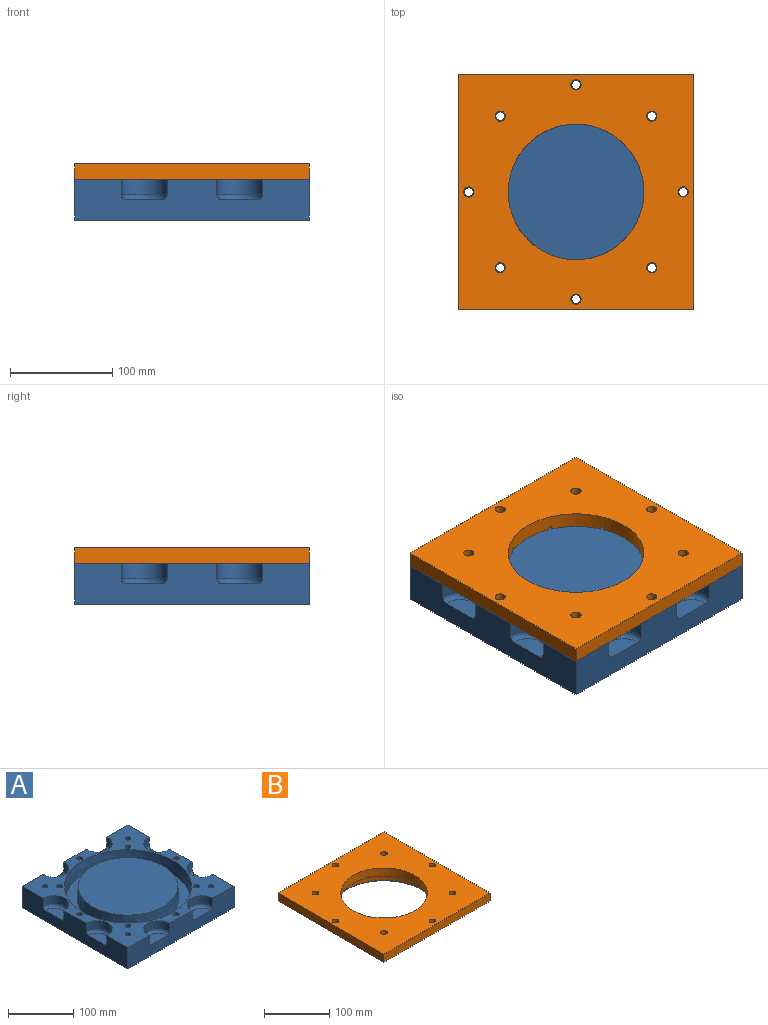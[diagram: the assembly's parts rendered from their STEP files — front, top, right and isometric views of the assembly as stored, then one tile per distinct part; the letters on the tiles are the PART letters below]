
ASSEMBLY  parts=2 mates=1
PART A: 46 faces, bbox 231.4x231.4x40 mm
  f0: plane 230x40mm, normal (0,1,0), area 7427.5mm2, adj f1,f15,f16,f17,f34,f35,f36,f37
  f1: plane 230x40mm, normal (-1,0,0), area 7427.5mm2, adj f0,f2,f16,f17,f30,f31,f32,f33
  f2: plane 230x40mm, normal (0,-1,0), area 7427.5mm2, adj f1,f15,f16,f17,f26,f27,f28,f29
  f3: cylinder r=4.3mm len=40mm, axis (0,0,1), area 1080.7mm2, adj f16,f17
  f4: cylinder r=4.3mm len=40mm, axis (0,0,1), area 1080.7mm2, adj f16,f17
  f5: cylinder r=4.3mm len=40mm, axis (0,0,1), area 1080.7mm2, adj f16,f17
  f6: cylinder r=4.3mm len=40mm, axis (0,0,1), area 1080.7mm2, adj f16,f17
  f7: cylinder r=4.3mm len=40mm, axis (0,0,1), area 1080.7mm2, adj f16,f17
  f8: cylinder r=4.3mm len=40mm, axis (0,0,1), area 1080.7mm2, adj f16,f17
  f9: cylinder r=4.3mm len=40mm, axis (0,0,1), area 1080.7mm2, adj f16,f17
  f10: cylinder r=4.3mm len=40mm, axis (0,0,1), area 1080.7mm2, adj f16,f17
  f11: cylinder r=4.3mm len=40mm, axis (0,0,1), area 1080.7mm2, adj f16,f17
  f12: cylinder r=4.3mm len=40mm, axis (0,0,1), area 1080.7mm2, adj f16,f17
  f13: cylinder r=4.3mm len=40mm, axis (0,0,1), area 1080.7mm2, adj f16,f17
  f14: cylinder r=4.3mm len=40mm, axis (0,0,1), area 1080.7mm2, adj f16,f17
  f15: plane 230x40mm, normal (1,0,0), area 7427.5mm2, adj f0,f2,f16,f17,f22,f23,f24,f25
  f16: plane 230x230mm, normal (0,0,-1), area 52202.9mm2, adj f0,f1,f2,f3,f4,f5,f6,f7
  f17: plane 230x230mm, normal (0,0,1), area 15320.3mm2, adj f0,f1,f2,f3,f4,f5,f6,f7
  f18: cone r=76.5mm half-angle=3deg, axis (0,0,-1), area 12136.1mm2, adj f20,f21
  f19: cone r=97.5mm half-angle=3deg, axis (0,0,1), area 15233.2mm2, adj f17,f20
  f20: plane 192.38x192.38mm, normal (0,0,1), area 10047mm2, adj f18,f19
  f21: plane 153x153mm, normal (0,0,1), area 18385.4mm2, adj f18
  f22: plane 35x19.32mm, normal (0,0,1), area 544.8mm2, adj f15,f43
  f23: cylinder r=22.5mm len=45mm, axis (0,0,1), area 1115.1mm2, adj f15,f17,f43
  f24: plane 35x19.32mm, normal (0,0,1), area 544.8mm2, adj f15,f42
  f25: cylinder r=22.5mm len=45mm, axis (0,0,1), area 1115.1mm2, adj f15,f17,f42
  f26: cylinder r=22.5mm len=45mm, axis (0,0,1), area 1115.1mm2, adj f2,f17,f45
  f27: plane 35x19.32mm, normal (0,0,1), area 544.8mm2, adj f2,f45
  f28: cylinder r=22.5mm len=45mm, axis (0,0,1), area 1115.1mm2, adj f2,f17,f44
  f29: plane 35x19.32mm, normal (0,0,1), area 544.8mm2, adj f2,f44
  f30: cylinder r=22.5mm len=45mm, axis (0,0,1), area 1115.1mm2, adj f1,f17,f39
  f31: plane 35x19.32mm, normal (0,0,1), area 544.8mm2, adj f1,f39
  f32: cylinder r=22.5mm len=45mm, axis (0,0,1), area 1115.1mm2, adj f1,f17,f38
  f33: plane 35x19.32mm, normal (0,0,1), area 544.8mm2, adj f1,f38
  f34: plane 35x19.32mm, normal (0,0,1), area 544.8mm2, adj f0,f41
  f35: cylinder r=22.5mm len=45mm, axis (0,0,1), area 1115.1mm2, adj f0,f17,f41
  f36: plane 35x19.32mm, normal (0,0,1), area 544.8mm2, adj f0,f40
  f37: cylinder r=22.5mm len=45mm, axis (0,0,1), area 1115.1mm2, adj f0,f17,f40
  f38: torus R=17.5mm, axis (0,0,1), area 539mm2, adj f1,f32,f33
  f39: torus R=17.5mm, axis (0,0,1), area 539mm2, adj f1,f30,f31
  f40: torus R=17.5mm, axis (0,0,1), area 539mm2, adj f0,f36,f37
  f41: torus R=17.5mm, axis (0,0,1), area 539mm2, adj f0,f34,f35
  f42: torus R=17.5mm, axis (0,0,1), area 539mm2, adj f15,f24,f25
  f43: torus R=17.5mm, axis (0,0,1), area 539mm2, adj f15,f22,f23
  f44: torus R=17.5mm, axis (0,0,1), area 539mm2, adj f2,f28,f29
  f45: torus R=17.5mm, axis (0,0,1), area 539mm2, adj f2,f26,f27
PART B: 152 faces, bbox 230x230x35 mm
  f0: plane 161x161mm, normal (0,0,-1), area 1814.9mm2, adj f24,f25,f26,f27,f28,f29,f30,f31
  f1: plane 230x230mm, normal (0,0,-1), area 22138.5mm2, adj f11,f12,f13,f14,f15,f16,f17,f18
  f2: plane 43.26x43.26mm, normal (0,0,-1), area 531.6mm2, adj f9,f36,f57,f61,f100,f101
  f3: plane 55.77x14.5mm, normal (0,0,-1), area 531.6mm2, adj f9,f38,f94,f95,f102,f103
  f4: plane 43.26x43.26mm, normal (0,0,-1), area 531.6mm2, adj f9,f24,f89,f90,f96,f97
  f5: plane 55.77x14.5mm, normal (0,0,-1), area 531.6mm2, adj f9,f26,f83,f84,f87,f91
  f6: plane 43.26x43.26mm, normal (0,0,-1), area 531.6mm2, adj f9,f28,f77,f78,f81,f85
  f7: plane 55.77x14.5mm, normal (0,0,-1), area 531.6mm2, adj f9,f30,f71,f72,f75,f79
  f8: plane 43.26x43.26mm, normal (0,0,-1), area 531.6mm2, adj f9,f32,f65,f66,f69,f73
  f9: cylinder r=66.5mm len=133mm, axis (0,0,-1), area 6195.5mm2, adj f2,f3,f4,f5,f6,f7,f8,f10
  f10: plane 55.77x14.5mm, normal (0,0,-1), area 531.6mm2, adj f9,f34,f59,f60,f63,f67
  f11: plane 230x15mm, normal (0,1,0), area 3450mm2, adj f1,f12,f14,f23
  f12: plane 230x15mm, normal (-1,0,0), area 3450mm2, adj f1,f11,f13,f23
  f13: plane 230x15mm, normal (0,-1,0), area 3450mm2, adj f1,f12,f14,f23
  f14: plane 230x15mm, normal (1,0,0), area 3450mm2, adj f1,f11,f13,f23
  f15: cylinder r=5mm len=15mm, axis (0,0,-1), area 471.2mm2, adj f1,f23
  f16: cylinder r=5mm len=15mm, axis (0,0,-1), area 471.2mm2, adj f1,f23
  f17: cylinder r=5mm len=15mm, axis (0,0,-1), area 471.2mm2, adj f1,f23
  f18: cylinder r=5mm len=15mm, axis (0,0,-1), area 471.2mm2, adj f1,f23
  f19: cylinder r=5mm len=15mm, axis (0,0,-1), area 471.2mm2, adj f1,f23
  f20: cylinder r=5mm len=15mm, axis (0,0,-1), area 471.2mm2, adj f1,f23
  f21: cylinder r=5mm len=15mm, axis (0,0,-1), area 471.2mm2, adj f1,f23
  f22: cylinder r=5mm len=15mm, axis (0,0,-1), area 471.2mm2, adj f1,f23
  f23: plane 230x230mm, normal (0,0,1), area 38378.8mm2, adj f9,f11,f12,f13,f14,f15,f16,f17
  f24: cone r=76.5mm half-angle=3deg, axis (0,0,-1), area 285.1mm2, adj f0,f4,f25,f55
  f25: cone r=1.5mm half-angle=3deg, axis (0,0,-1), area 24.6mm2, adj f0,f24,f26,f88
  f26: cone r=76.5mm half-angle=3deg, axis (0,0,-1), area 285.1mm2, adj f0,f5,f25,f27
  f27: cone r=1.5mm half-angle=3deg, axis (0,0,-1), area 24.6mm2, adj f0,f26,f28,f82
  f28: cone r=76.5mm half-angle=3deg, axis (0,0,-1), area 285.1mm2, adj f0,f6,f27,f29
  f29: cone r=1.5mm half-angle=3deg, axis (0,0,-1), area 24.6mm2, adj f0,f28,f30,f76
  f30: cone r=76.5mm half-angle=3deg, axis (0,0,-1), area 285.1mm2, adj f0,f7,f29,f31
  f31: cone r=1.5mm half-angle=3deg, axis (0,0,-1), area 24.6mm2, adj f0,f30,f32,f70
  f32: cone r=76.5mm half-angle=3deg, axis (0,0,-1), area 285.1mm2, adj f0,f8,f31,f33
  f33: cone r=1.5mm half-angle=3deg, axis (0,0,-1), area 24.6mm2, adj f0,f32,f34,f64
  f34: cone r=76.5mm half-angle=3deg, axis (0,0,-1), area 285.1mm2, adj f0,f10,f33,f35
  f35: cone r=1.5mm half-angle=3deg, axis (0,0,-1), area 24.6mm2, adj f0,f34,f36,f58
  f36: cone r=76.5mm half-angle=3deg, axis (0,0,-1), area 285.1mm2, adj f0,f2,f35,f37
  f37: cone r=1.5mm half-angle=3deg, axis (0,0,-1), area 24.6mm2, adj f0,f36,f38,f99
  f38: cone r=76.5mm half-angle=3deg, axis (0,0,-1), area 285.1mm2, adj f0,f3,f37,f55
  f39: cone r=1.5mm half-angle=3deg, axis (0,0,-1), area 24.3mm2, adj f40,f54,f56,f111
  f40: cone r=97.5mm half-angle=3deg, axis (0,0,1), area 366.7mm2, adj f1,f39,f41,f56
  f41: cone r=1.5mm half-angle=3deg, axis (0,0,-1), area 24.3mm2, adj f40,f42,f56,f106
  f42: cone r=97.5mm half-angle=3deg, axis (0,0,1), area 366.7mm2, adj f1,f41,f43,f56
  f43: cone r=1.5mm half-angle=3deg, axis (0,0,-1), area 24.3mm2, adj f42,f44,f56,f141
  f44: cone r=97.5mm half-angle=3deg, axis (0,0,1), area 366.7mm2, adj f1,f43,f45,f56
  f45: cone r=1.5mm half-angle=3deg, axis (0,0,-1), area 24.3mm2, adj f44,f46,f56,f136
  f46: cone r=97.5mm half-angle=3deg, axis (0,0,1), area 366.7mm2, adj f1,f45,f47,f56
  f47: cone r=1.5mm half-angle=3deg, axis (0,0,-1), area 24.3mm2, adj f46,f48,f56,f131
  f48: cone r=97.5mm half-angle=3deg, axis (0,0,1), area 366.7mm2, adj f1,f47,f49,f56
  f49: cone r=1.5mm half-angle=3deg, axis (0,0,-1), area 24.3mm2, adj f48,f50,f56,f126
  f50: cone r=97.5mm half-angle=3deg, axis (0,0,1), area 366.7mm2, adj f1,f49,f51,f56
  f51: cone r=1.5mm half-angle=3deg, axis (0,0,-1), area 24.3mm2, adj f50,f52,f56,f121
  f52: cone r=97.5mm half-angle=3deg, axis (0,0,1), area 366.7mm2, adj f1,f51,f53,f56
  f53: cone r=1.5mm half-angle=3deg, axis (0,0,-1), area 24.3mm2, adj f52,f54,f56,f116
  f54: cone r=97.5mm half-angle=3deg, axis (0,0,1), area 366.7mm2, adj f1,f39,f53,f56
  f55: cone r=1.5mm half-angle=3deg, axis (0,0,-1), area 24.6mm2, adj f0,f24,f38,f93
  f56: plane 194.48x194.48mm, normal (0,0,-1), area 2208.4mm2, adj f39,f40,f41,f42,f43,f44,f45,f46
  f57: plane 9.23x3.82mm, normal (0.38,0.92,0), area 30mm2, adj f2,f58,f61,f62
  f58: cylinder r=1.5mm len=3mm, axis (0,0,-1), area 14.2mm2, adj f35,f57,f59,f62
  f59: plane 9.23x3.82mm, normal (-0.38,-0.92,0), area 30mm2, adj f10,f58,f60,f62
  f60: cylinder r=1.5mm len=3mm, axis (0,0,-1), area 0.1mm2, adj f9,f10,f59,f62
  f61: cylinder r=1.5mm len=3mm, axis (0,0,-1), area 0.1mm2, adj f2,f9,f57,f62
  f62: plane 11.33x6.72mm, normal (0,0,-1), area 33.6mm2, adj f9,f57,f58,f59,f60,f61
  f63: plane 9.23x3.82mm, normal (-0.38,0.92,0), area 30mm2, adj f10,f64,f67,f68
  f64: cylinder r=1.5mm len=3mm, axis (0,0,-1), area 14.2mm2, adj f33,f63,f65,f68
  f65: plane 9.23x3.82mm, normal (0.38,-0.92,0), area 30mm2, adj f8,f64,f66,f68
  f66: cylinder r=1.5mm len=3mm, axis (0,0,-1), area 0.1mm2, adj f8,f9,f65,f68
  f67: cylinder r=1.5mm len=3mm, axis (0,0,-1), area 0.1mm2, adj f9,f10,f63,f68
  f68: plane 11.33x6.72mm, normal (0,0,-1), area 33.6mm2, adj f9,f63,f64,f65,f66,f67
  f69: plane 9.23x3.82mm, normal (-0.92,0.38,0), area 30mm2, adj f8,f70,f73,f74
  f70: cylinder r=1.5mm len=3mm, axis (0,0,-1), area 14.2mm2, adj f31,f69,f71,f74
  f71: plane 9.23x3.82mm, normal (0.92,-0.38,0), area 30mm2, adj f7,f70,f72,f74
  f72: cylinder r=1.5mm len=3mm, axis (0,0,-1), area 0.1mm2, adj f7,f9,f71,f74
  f73: cylinder r=1.5mm len=3mm, axis (0,0,-1), area 0.1mm2, adj f8,f9,f69,f74
  f74: plane 11.33x6.72mm, normal (0,0,-1), area 33.6mm2, adj f9,f69,f70,f71,f72,f73
  f75: plane 9.23x3.82mm, normal (-0.92,-0.38,0), area 30mm2, adj f7,f76,f79,f80
  f76: cylinder r=1.5mm len=3mm, axis (0,0,-1), area 14.2mm2, adj f29,f75,f77,f80
  f77: plane 9.23x3.82mm, normal (0.92,0.38,0), area 30mm2, adj f6,f76,f78,f80
  f78: cylinder r=1.5mm len=3mm, axis (0,0,-1), area 0.1mm2, adj f6,f9,f77,f80
  f79: cylinder r=1.5mm len=3mm, axis (0,0,-1), area 0.1mm2, adj f7,f9,f75,f80
  f80: plane 11.33x6.72mm, normal (0,0,-1), area 33.6mm2, adj f9,f75,f76,f77,f78,f79
  f81: plane 9.23x3.82mm, normal (-0.38,-0.92,0), area 30mm2, adj f6,f82,f85,f86
  f82: cylinder r=1.5mm len=3mm, axis (0,0,-1), area 14.2mm2, adj f27,f81,f83,f86
  f83: plane 9.23x3.82mm, normal (0.38,0.92,0), area 30mm2, adj f5,f82,f84,f86
  f84: cylinder r=1.5mm len=3mm, axis (0,0,-1), area 0.1mm2, adj f5,f9,f83,f86
  f85: cylinder r=1.5mm len=3mm, axis (0,0,-1), area 0.1mm2, adj f6,f9,f81,f86
  f86: plane 11.33x6.72mm, normal (0,0,-1), area 33.6mm2, adj f9,f81,f82,f83,f84,f85
  f87: plane 9.23x3.82mm, normal (0.38,-0.92,0), area 30mm2, adj f5,f88,f91,f92
  f88: cylinder r=1.5mm len=3mm, axis (0,0,-1), area 14.2mm2, adj f25,f87,f89,f92
  f89: plane 9.23x3.82mm, normal (-0.38,0.92,0), area 30mm2, adj f4,f88,f90,f92
  f90: cylinder r=1.5mm len=3mm, axis (0,0,-1), area 0.1mm2, adj f4,f9,f89,f92
  f91: cylinder r=1.5mm len=3mm, axis (0,0,-1), area 0.1mm2, adj f5,f9,f87,f92
  f92: plane 11.33x6.72mm, normal (0,0,-1), area 33.6mm2, adj f9,f87,f88,f89,f90,f91
  f93: cylinder r=1.5mm len=3mm, axis (0,0,-1), area 14.2mm2, adj f55,f94,f97,f98
  f94: plane 9.23x3.82mm, normal (-0.92,0.38,0), area 30mm2, adj f3,f93,f95,f98
  f95: cylinder r=1.5mm len=3mm, axis (0,0,-1), area 0.1mm2, adj f3,f9,f94,f98
  f96: cylinder r=1.5mm len=3mm, axis (0,0,-1), area 0.1mm2, adj f4,f9,f97,f98
  f97: plane 9.23x3.82mm, normal (0.92,-0.38,0), area 30mm2, adj f4,f93,f96,f98
  f98: plane 11.33x6.72mm, normal (0,0,-1), area 33.6mm2, adj f9,f93,f94,f95,f96,f97
  f99: cylinder r=1.5mm len=3mm, axis (0,0,-1), area 14.2mm2, adj f37,f100,f103,f104
  f100: plane 9.23x3.82mm, normal (-0.92,-0.38,0), area 30mm2, adj f2,f99,f101,f104
  f101: cylinder r=1.5mm len=3mm, axis (0,0,-1), area 0.1mm2, adj f2,f9,f100,f104
  f102: cylinder r=1.5mm len=3mm, axis (0,0,-1), area 0.1mm2, adj f3,f9,f103,f104
  f103: plane 9.23x3.82mm, normal (0.92,0.38,0), area 30mm2, adj f3,f99,f102,f104
  f104: plane 11.33x6.72mm, normal (0,0,-1), area 33.6mm2, adj f9,f99,f100,f101,f102,f103
  f105: plane 9.25x3.83mm, normal (-0.38,-0.92,0), area 30mm2, adj f1,f106,f108,f109
  f106: cylinder r=1.5mm len=3mm, axis (0,0,-1), area 14.1mm2, adj f1,f41,f105,f107,f109
  f107: plane 9.24x3.83mm, normal (0.38,0.92,0), area 30mm2, adj f1,f106,f108,f109
  f108: cylinder r=1.5mm len=3mm, axis (0,0,-1), area 14.1mm2, adj f1,f105,f107,f109
  f109: plane 12.24x6.83mm, normal (0,0,-1), area 37.1mm2, adj f105,f106,f107,f108
  f110: plane 9.25x3.83mm, normal (-0.92,-0.38,0), area 30mm2, adj f1,f111,f113,f114
  f111: cylinder r=1.5mm len=3mm, axis (0,0,-1), area 14.1mm2, adj f1,f39,f110,f112,f114
  f112: plane 9.24x3.83mm, normal (0.92,0.38,0), area 30mm2, adj f1,f111,f113,f114
  f113: cylinder r=1.5mm len=3mm, axis (0,0,-1), area 14.1mm2, adj f1,f110,f112,f114
  f114: plane 12.24x6.83mm, normal (0,0,-1), area 37.1mm2, adj f110,f111,f112,f113
  f115: plane 9.25x3.83mm, normal (-0.92,0.38,0), area 30mm2, adj f1,f116,f118,f119
  f116: cylinder r=1.5mm len=3mm, axis (0,0,-1), area 14.1mm2, adj f1,f53,f115,f117,f119
  f117: plane 9.24x3.83mm, normal (0.92,-0.38,0), area 30mm2, adj f1,f116,f118,f119
  f118: cylinder r=1.5mm len=3mm, axis (0,0,-1), area 14.1mm2, adj f1,f115,f117,f119
  f119: plane 12.24x6.83mm, normal (0,0,-1), area 37.1mm2, adj f115,f116,f117,f118
  f120: plane 9.25x3.83mm, normal (-0.38,0.92,0), area 30mm2, adj f1,f121,f123,f124
  f121: cylinder r=1.5mm len=3mm, axis (0,0,-1), area 14.1mm2, adj f1,f51,f120,f122,f124
  f122: plane 9.24x3.83mm, normal (0.38,-0.92,0), area 30mm2, adj f1,f121,f123,f124
  f123: cylinder r=1.5mm len=3mm, axis (0,0,-1), area 14.1mm2, adj f1,f120,f122,f124
  f124: plane 12.24x6.83mm, normal (0,0,-1), area 37.1mm2, adj f120,f121,f122,f123
  f125: plane 9.25x3.83mm, normal (0.38,0.92,0), area 30mm2, adj f1,f126,f128,f129
  f126: cylinder r=1.5mm len=3mm, axis (0,0,-1), area 14.1mm2, adj f1,f49,f125,f127,f129
  f127: plane 9.24x3.83mm, normal (-0.38,-0.92,0), area 30mm2, adj f1,f126,f128,f129
  f128: cylinder r=1.5mm len=3mm, axis (0,0,-1), area 14.1mm2, adj f1,f125,f127,f129
  f129: plane 12.24x6.83mm, normal (0,0,-1), area 37.1mm2, adj f125,f126,f127,f128
  f130: plane 9.25x3.83mm, normal (0.92,0.38,0), area 30mm2, adj f1,f131,f133,f134
  f131: cylinder r=1.5mm len=3mm, axis (0,0,-1), area 14.1mm2, adj f1,f47,f130,f132,f134
  f132: plane 9.24x3.83mm, normal (-0.92,-0.38,0), area 30mm2, adj f1,f131,f133,f134
  f133: cylinder r=1.5mm len=3mm, axis (0,0,-1), area 14.1mm2, adj f1,f130,f132,f134
  f134: plane 12.24x6.83mm, normal (0,0,-1), area 37.1mm2, adj f130,f131,f132,f133
  f135: plane 9.25x3.83mm, normal (0.92,-0.38,0), area 30mm2, adj f1,f136,f138,f139
  f136: cylinder r=1.5mm len=3mm, axis (0,0,-1), area 14.1mm2, adj f1,f45,f135,f137,f139
  f137: plane 9.24x3.83mm, normal (-0.92,0.38,0), area 30mm2, adj f1,f136,f138,f139
  f138: cylinder r=1.5mm len=3mm, axis (0,0,-1), area 14.1mm2, adj f1,f135,f137,f139
  f139: plane 12.24x6.83mm, normal (0,0,-1), area 37.1mm2, adj f135,f136,f137,f138
  f140: plane 9.25x3.83mm, normal (0.38,-0.92,0), area 30mm2, adj f1,f141,f143,f144
  f141: cylinder r=1.5mm len=3mm, axis (0,0,-1), area 14.1mm2, adj f1,f43,f140,f142,f144
  f142: plane 9.24x3.83mm, normal (-0.38,0.92,0), area 30mm2, adj f1,f141,f143,f144
  f143: cylinder r=1.5mm len=3mm, axis (0,0,-1), area 14.1mm2, adj f1,f140,f142,f144
  f144: plane 12.24x6.83mm, normal (0,0,-1), area 37.1mm2, adj f140,f141,f142,f143
  f145: cylinder r=81.5mm len=163mm, axis (0,0,1), area 6657mm2, adj f149,f150
  f146: cylinder r=92.5mm len=185mm, axis (0,0,1), area 7555.5mm2, adj f148,f151
  f147: plane 183x183mm, normal (0,0,-1), area 4919.7mm2, adj f150,f151
  f148: torus R=93.5mm, axis (0,0,1), area 916.5mm2, adj f56,f146
  f149: torus R=80.5mm, axis (0,0,1), area 800.8mm2, adj f0,f145
  f150: torus R=82.5mm, axis (0,0,1), area 808mm2, adj f145,f147
  f151: torus R=91.5mm, axis (0,0,1), area 909.4mm2, adj f146,f147
PLACE A t=(-15,0,0)mm
PLACE B t=(-15,0,0)mm
MATE fastened A.f3 <-> B.f22  axis (0,0,1) through (90,0,0)mm
